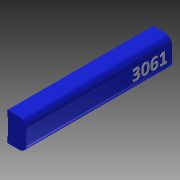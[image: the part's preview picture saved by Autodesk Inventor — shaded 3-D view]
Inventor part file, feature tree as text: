
AUTODESK INVENTOR PART (.ipt)
format: ipt  version: 2013 (Build 170138000, 138)  size: 301,056 bytes
history: native  units: in
note: dims shown in document units (in); Inventor stores cm internally (conversion verified against a paired STEP export)
features: extrude x4, reference x4, sketch x3, projected_geometry x1
ambient origin geometry x8: Origin, YZ Plane, XZ Plane, XY Plane, X Axis, Y Axis, Z Axis, Center Point
bodies: Solid1 (feature_tree)
feature tree (12):
  sketch  "Sketch1"  dims[d0=0.0625in d1=0.0in d3=1.0in]
  extrude  "Extrusion1"  Depth=1.0in
  extrude  "Extrusion2"  Depth=0.0625in
  extrude  "Extrusion3"  Depth=0.0625in TaperAngle=0.0deg
  extrude  "Extrusion5"  Depth=6.0in
  reference  "Reference4"
  reference  "Reference5"
  sketch  "Sketch2"  dims[d7=1.0in d9=0.0625in]
  sketch  "Sketch3"  dims[d10=25.875in d11=0.0in d12=0.0625in d13=0.0in d42=6.0in d43=0.0625in d44=0.0in d45=0.0625in d46=0.0625in d47=1.0in d48=2.5in]
  reference  "Reference6"
  projected_geometry  "Projected Loop1"
  reference  "Reference7"
